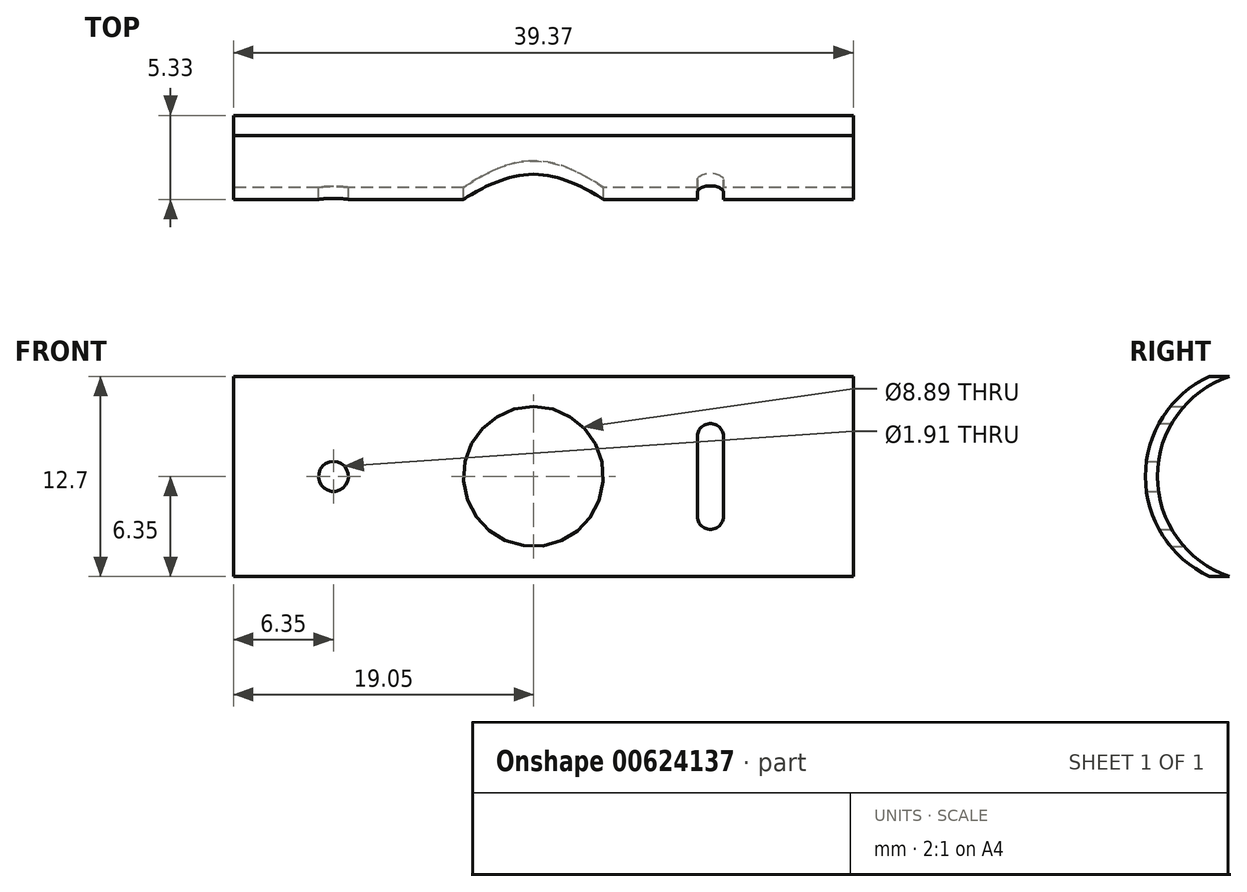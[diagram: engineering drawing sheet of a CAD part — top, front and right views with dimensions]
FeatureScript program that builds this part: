
annotation { "Feature Type Name" : "Feature", "Feature Type Description" : "" }
export const myFeature = defineFeature(function(context is Context, id is Id, definition is map)
    precondition{}
    {
        {
            var Q0;
            Q0=qCreatedBy(makeId("Right.planeOp"),FACE);
            var sketch = newSketch(context, id + "F0", { "sketchPlane" : qUnion([Q0])});
            skLineSegment(sketch, "E0", {"start": v(0, 0) * mm, "end": v(-1.27, 0) * mm});
            skLineSegment(sketch, "E1", {"start": v(0, 12.7) * mm, "end": v(-1.27, 12.7) * mm});
            skArc(sketch, "E2", {"start": v(0, 12.7) * mm, "mid": v(-4.57, 6.35) * mm, "end": v(0, 0) * mm});
            skArc(sketch, "E3", {"start": v(-1.27, 12.7) * mm, "mid": v(-5.33, 6.35) * mm, "end": v(-1.27, 0) * mm});
            skSolve(sketch);
        }
        {
            var Q0;
            Q0=makeQuery(id+"F0.imprint","IMPRINT",FACE,{"disambiguationData":[TD([[makeQuery(id+"F0.imprint","IMPRINT",EDGE,{"derivedFrom":sQuery(id+"F0.wireOp",EDGE,"E0")}),-1.0]])]});
            extrude(context, id + "F1", {"entities" : qUnion([Q0]), "depth" : 39.37 * mm, "offsetDistance" : 25.4 * mm});
        }
        {
            var Q0;
            Q0=qCreatedBy(makeId("Front.planeOp"),FACE);
            var sketch = newSketch(context, id + "F2", { "sketchPlane" : qUnion([Q0])});
            skPoint(sketch, "E4", {"position": v(19.05, 6.35) * mm});
            skPoint(sketch, "E5", {"position": v(6.35, 6.35) * mm});
            skLineSegment(sketch, "E6", {"start": v(29.46, 6.35) * mm, "end": v(29.46, 8.9) * mm});
            skLineSegment(sketch, "E7", {"start": v(29.46, 6.35) * mm, "end": v(29.46, 3.81) * mm});
            skLineSegment(sketch, "E8", {"start": v(31.12, 8.9) * mm, "end": v(31.12, 6.35) * mm});
            skLineSegment(sketch, "E9", {"start": v(31.12, 6.35) * mm, "end": v(31.12, 3.81) * mm});
            skArc(sketch, "E10", {"start": v(31.12, 8.9) * mm, "mid": v(30.29, 9.72) * mm, "end": v(29.46, 8.9) * mm});
            skArc(sketch, "E11", {"start": v(29.46, 3.81) * mm, "mid": v(30.29, 2.98) * mm, "end": v(31.12, 3.81) * mm});
            skSolve(sketch);
        }
        {
            var Q0;
            Q0=sQuery(id+"F2.wireOp",VERTEX,"E4");
            var Q1;
            Q1=makeQuery(id+"F1.opExtrude","SWEPT_BODY",BODY,{"disambiguationData":[OSD([sQuery(id+"F0.wireOp",EDGE,"E0"),sQuery(id+"F0.wireOp",EDGE,"E1"),sQuery(id+"F0.wireOp",EDGE,"E2"),sQuery(id+"F0.wireOp",EDGE,"E3")])]});
            hole(context, id + "F3", {"style" : HoleStyle.SIMPLE, "endStyle" : HoleEndStyle.THROUGH, "oppositeDirection" : true, "holeDiameter" : 8.9 * mm, "majorDiameter" : 6.35 * mm, "isTappedThrough" : true, "tappedDepth" : 12.7 * mm, "tapClearance" : 3, "locations" : qUnion([Q0]), "scope" : qUnion([Q1])});
        }
        {
            var Q0;
            Q0=qCreatedBy(makeId("Front.planeOp"),FACE);
            var sketch = newSketch(context, id + "F4", { "sketchPlane" : qUnion([Q0])});
            skPoint(sketch, "E12", {"position": v(6.35, 6.35) * mm});
            skSolve(sketch);
        }
        {
            var Q0;
            Q0=sQuery(id+"F4.wireOp",VERTEX,"E12");
            var Q1;
            Q1=makeQuery(id+"F1.opExtrude","SWEPT_BODY",BODY,{"disambiguationData":[OSD([sQuery(id+"F0.wireOp",EDGE,"E0"),sQuery(id+"F0.wireOp",EDGE,"E1"),sQuery(id+"F0.wireOp",EDGE,"E2"),sQuery(id+"F0.wireOp",EDGE,"E3")])]});
            hole(context, id + "F5", {"style" : HoleStyle.SIMPLE, "endStyle" : HoleEndStyle.THROUGH, "oppositeDirection" : true, "holeDiameter" : 1.9 * mm, "majorDiameter" : 6.35 * mm, "isTappedThrough" : true, "tappedDepth" : 12.7 * mm, "tapClearance" : 3, "locations" : qUnion([Q0]), "scope" : qUnion([Q1])});
        }
        {
            var Q0;
            Q0=qCreatedBy(makeId("Front.planeOp"),FACE);
            var sketch = newSketch(context, id + "F6", { "sketchPlane" : qUnion([Q0])});
            skLineSegment(sketch, "E13", {"start": v(29.46, 6.35) * mm, "end": v(29.46, 8.9) * mm});
            skLineSegment(sketch, "E14", {"start": v(29.46, 6.35) * mm, "end": v(29.46, 3.81) * mm});
            skLineSegment(sketch, "E15", {"start": v(31.12, 8.9) * mm, "end": v(31.12, 6.35) * mm});
            skLineSegment(sketch, "E16", {"start": v(31.12, 6.35) * mm, "end": v(31.12, 3.81) * mm});
            skArc(sketch, "E17", {"start": v(31.12, 8.9) * mm, "mid": v(30.29, 9.72) * mm, "end": v(29.46, 8.9) * mm});
            skArc(sketch, "E18", {"start": v(29.46, 3.81) * mm, "mid": v(30.29, 2.98) * mm, "end": v(31.11, 3.81) * mm});
            skSolve(sketch);
        }
        {
            var Q0;
            Q0=makeQuery(id+"F6.imprint","IMPRINT",FACE,{"disambiguationData":[TD([[makeQuery(id+"F6.imprint","IMPRINT",EDGE,{"derivedFrom":sQuery(id+"F6.wireOp",EDGE,"E13")}),-1.0]])]});
            extrude(context, id + "F7", {"entities" : qUnion([Q0]), "operationType" : NewBodyOperationType.REMOVE, "depth" : 16 * mm, "offsetDistance" : 25.4 * mm});
        }
    });
